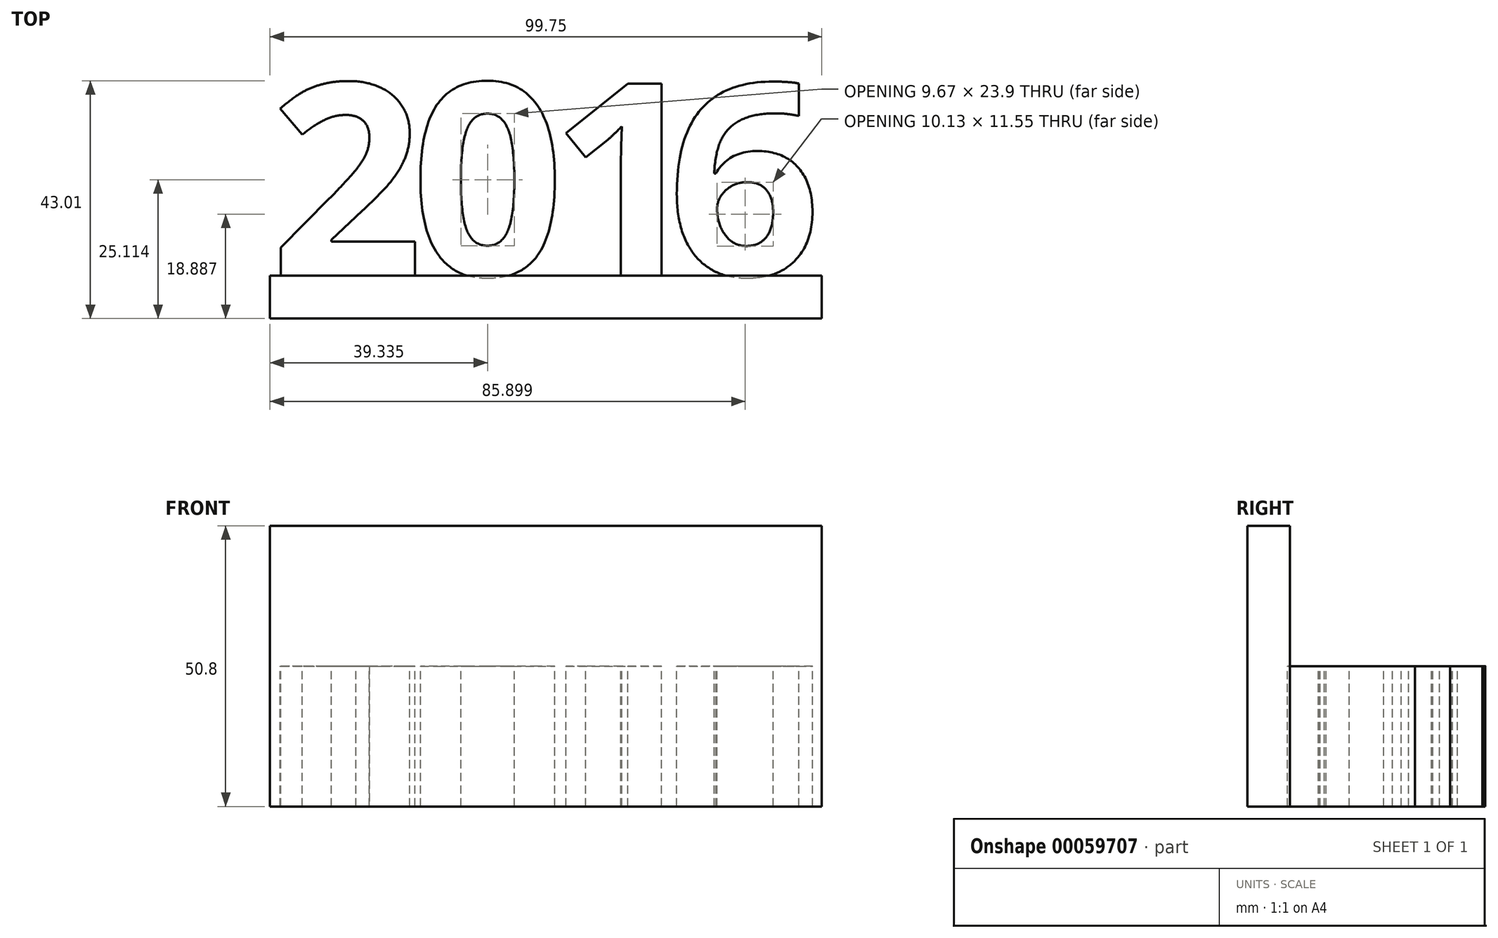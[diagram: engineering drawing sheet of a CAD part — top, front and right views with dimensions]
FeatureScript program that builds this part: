
annotation { "Feature Type Name" : "Feature", "Feature Type Description" : "" }
export const myFeature = defineFeature(function(context is Context, id is Id, definition is map)
    precondition{}
    {
        {
            var Q0;
            Q0=qCreatedBy(makeId("Top.planeOp"),FACE);
            var sketch = newSketch(context, id + "F0", { "sketchPlane" : qUnion([Q0])});
            skText(sketch, "E0", { "text": "2016", "fontName": "OpenSans-Bold.ttf"});
            const initialGuessF0  = {"E0": [0, 0, 1, 0, 0.03504]};
            skSetInitialGuess(sketch, initialGuessF0);
            skSolve(sketch);
        }
        {
            var Q0;
            Q0=makeQuery(id+"F0.imprint","IMPRINT",FACE,{"disambiguationData":[TD([[makeQuery(id+"F0.imprint","IMPRINT",EDGE,{"derivedFrom":sQuery(id+"F0.wireOp",EDGE,"E0.sketch_text.stroke-0")}),-1.0]])]});
            extrude(context, id + "F1", {"entities" : qUnion([Q0]), "oppositeDirection" : true, "depth" : 25.4 * mm});
        }
        {
            var Q0;
            Q0=makeQuery(id+"F0.imprint","IMPRINT",FACE,{"disambiguationData":[TD([[makeQuery(id+"F0.imprint","IMPRINT",EDGE,{"derivedFrom":sQuery(id+"F0.wireOp",EDGE,"E0.sketch_text.stroke-24")}),-1.0]])]});
            var Q1;
            Q1=makeQuery(id+"F0.imprint","IMPRINT",FACE,{"disambiguationData":[TD([[makeQuery(id+"F0.imprint","IMPRINT",EDGE,{"derivedFrom":sQuery(id+"F0.wireOp",EDGE,"E0.sketch_text.stroke-40")}),-1.0]])]});
            var Q2;
            Q2=makeQuery(id+"F0.imprint","IMPRINT",FACE,{"disambiguationData":[TD([[makeQuery(id+"F0.imprint","IMPRINT",EDGE,{"derivedFrom":sQuery(id+"F0.wireOp",EDGE,"E0.sketch_text.stroke-50")}),-1.0]])]});
            extrude(context, id + "F2", {"entities" : qUnion([Q0, Q1, Q2]), "operationType" : NewBodyOperationType.ADD, "oppositeDirection" : true, "depth" : 25.4 * mm});
        }
        {
            var Q0;
            Q0=makeQuery(id+"F2.opExtrude","SWEPT_BODY",BODY,{"disambiguationData":[OSD([sQuery(id+"F0.wireOp",EDGE,"E0.sketch_text.stroke-50"),sQuery(id+"F0.wireOp",EDGE,"E0.sketch_text.stroke-51"),sQuery(id+"F0.wireOp",EDGE,"E0.sketch_text.stroke-52"),sQuery(id+"F0.wireOp",EDGE,"E0.sketch_text.stroke-53"),sQuery(id+"F0.wireOp",EDGE,"E0.sketch_text.stroke-54"),sQuery(id+"F0.wireOp",EDGE,"E0.sketch_text.stroke-55"),sQuery(id+"F0.wireOp",EDGE,"E0.sketch_text.stroke-56"),sQuery(id+"F0.wireOp",EDGE,"E0.sketch_text.stroke-57"),sQuery(id+"F0.wireOp",EDGE,"E0.sketch_text.stroke-58"),sQuery(id+"F0.wireOp",EDGE,"E0.sketch_text.stroke-59"),sQuery(id+"F0.wireOp",EDGE,"E0.sketch_text.stroke-60"),sQuery(id+"F0.wireOp",EDGE,"E0.sketch_text.stroke-61"),sQuery(id+"F0.wireOp",EDGE,"E0.sketch_text.stroke-62"),sQuery(id+"F0.wireOp",EDGE,"E0.sketch_text.stroke-63"),sQuery(id+"F0.wireOp",EDGE,"E0.sketch_text.stroke-64"),sQuery(id+"F0.wireOp",EDGE,"E0.sketch_text.stroke-65"),sQuery(id+"F0.wireOp",EDGE,"E0.sketch_text.stroke-66"),sQuery(id+"F0.wireOp",EDGE,"E0.sketch_text.stroke-67"),sQuery(id+"F0.wireOp",EDGE,"E0.sketch_text.stroke-68"),sQuery(id+"F0.wireOp",EDGE,"E0.sketch_text.stroke-69"),sQuery(id+"F0.wireOp",EDGE,"E0.sketch_text.stroke-70"),sQuery(id+"F0.wireOp",EDGE,"E0.sketch_text.stroke-71"),sQuery(id+"F0.wireOp",EDGE,"E0.sketch_text.stroke-72"),sQuery(id+"F0.wireOp",EDGE,"E0.sketch_text.stroke-73"),sQuery(id+"F0.wireOp",EDGE,"E0.sketch_text.stroke-74")])]});
            transform(context, id + "F3", {"entities" : qUnion([Q0]), "transformType" : TransformType.TRANSLATION_3D, "dx" : -4.65 * mm, "dy" : 0 * mm, "dz" : 0 * mm, "makeCopy" : false});
        }
        {
            var Q0;
            Q0=makeQuery(id+"F2.opExtrude","SWEPT_BODY",BODY,{"disambiguationData":[OSD([sQuery(id+"F0.wireOp",EDGE,"E0.sketch_text.stroke-24"),sQuery(id+"F0.wireOp",EDGE,"E0.sketch_text.stroke-25"),sQuery(id+"F0.wireOp",EDGE,"E0.sketch_text.stroke-26"),sQuery(id+"F0.wireOp",EDGE,"E0.sketch_text.stroke-27"),sQuery(id+"F0.wireOp",EDGE,"E0.sketch_text.stroke-28"),sQuery(id+"F0.wireOp",EDGE,"E0.sketch_text.stroke-29"),sQuery(id+"F0.wireOp",EDGE,"E0.sketch_text.stroke-30"),sQuery(id+"F0.wireOp",EDGE,"E0.sketch_text.stroke-31"),sQuery(id+"F0.wireOp",EDGE,"E0.sketch_text.stroke-32"),sQuery(id+"F0.wireOp",EDGE,"E0.sketch_text.stroke-33"),sQuery(id+"F0.wireOp",EDGE,"E0.sketch_text.stroke-34"),sQuery(id+"F0.wireOp",EDGE,"E0.sketch_text.stroke-35"),sQuery(id+"F0.wireOp",EDGE,"E0.sketch_text.stroke-36"),sQuery(id+"F0.wireOp",EDGE,"E0.sketch_text.stroke-37"),sQuery(id+"F0.wireOp",EDGE,"E0.sketch_text.stroke-38"),sQuery(id+"F0.wireOp",EDGE,"E0.sketch_text.stroke-39")])]});
            transform(context, id + "F4", {"entities" : qUnion([Q0]), "transformType" : TransformType.TRANSLATION_3D, "dx" : -2.34 * mm, "dy" : 0 * mm, "dz" : 0 * mm, "makeCopy" : false});
        }
        {
            var Q0;
            Q0=makeQuery(id+"F2.opExtrude","SWEPT_BODY",BODY,{"disambiguationData":[OSD([sQuery(id+"F0.wireOp",EDGE,"E0.sketch_text.stroke-40"),sQuery(id+"F0.wireOp",EDGE,"E0.sketch_text.stroke-41"),sQuery(id+"F0.wireOp",EDGE,"E0.sketch_text.stroke-42"),sQuery(id+"F0.wireOp",EDGE,"E0.sketch_text.stroke-43"),sQuery(id+"F0.wireOp",EDGE,"E0.sketch_text.stroke-44"),sQuery(id+"F0.wireOp",EDGE,"E0.sketch_text.stroke-45"),sQuery(id+"F0.wireOp",EDGE,"E0.sketch_text.stroke-46"),sQuery(id+"F0.wireOp",EDGE,"E0.sketch_text.stroke-47"),sQuery(id+"F0.wireOp",EDGE,"E0.sketch_text.stroke-48"),sQuery(id+"F0.wireOp",EDGE,"E0.sketch_text.stroke-49")])]});
            transform(context, id + "F5", {"entities" : qUnion([Q0]), "transformType" : TransformType.TRANSLATION_3D, "dx" : -4.9 * mm, "dy" : 0 * mm, "dz" : 0 * mm, "makeCopy" : false});
        }
        {
            var Q0;
            Q0=makeQuery(id+"F2.opExtrude","SWEPT_BODY",BODY,{"disambiguationData":[OSD([sQuery(id+"F0.wireOp",EDGE,"E0.sketch_text.stroke-50"),sQuery(id+"F0.wireOp",EDGE,"E0.sketch_text.stroke-51"),sQuery(id+"F0.wireOp",EDGE,"E0.sketch_text.stroke-52"),sQuery(id+"F0.wireOp",EDGE,"E0.sketch_text.stroke-53"),sQuery(id+"F0.wireOp",EDGE,"E0.sketch_text.stroke-54"),sQuery(id+"F0.wireOp",EDGE,"E0.sketch_text.stroke-55"),sQuery(id+"F0.wireOp",EDGE,"E0.sketch_text.stroke-56"),sQuery(id+"F0.wireOp",EDGE,"E0.sketch_text.stroke-57"),sQuery(id+"F0.wireOp",EDGE,"E0.sketch_text.stroke-58"),sQuery(id+"F0.wireOp",EDGE,"E0.sketch_text.stroke-59"),sQuery(id+"F0.wireOp",EDGE,"E0.sketch_text.stroke-60"),sQuery(id+"F0.wireOp",EDGE,"E0.sketch_text.stroke-61"),sQuery(id+"F0.wireOp",EDGE,"E0.sketch_text.stroke-62"),sQuery(id+"F0.wireOp",EDGE,"E0.sketch_text.stroke-63"),sQuery(id+"F0.wireOp",EDGE,"E0.sketch_text.stroke-64"),sQuery(id+"F0.wireOp",EDGE,"E0.sketch_text.stroke-65"),sQuery(id+"F0.wireOp",EDGE,"E0.sketch_text.stroke-66"),sQuery(id+"F0.wireOp",EDGE,"E0.sketch_text.stroke-67"),sQuery(id+"F0.wireOp",EDGE,"E0.sketch_text.stroke-68"),sQuery(id+"F0.wireOp",EDGE,"E0.sketch_text.stroke-69"),sQuery(id+"F0.wireOp",EDGE,"E0.sketch_text.stroke-70"),sQuery(id+"F0.wireOp",EDGE,"E0.sketch_text.stroke-71"),sQuery(id+"F0.wireOp",EDGE,"E0.sketch_text.stroke-72"),sQuery(id+"F0.wireOp",EDGE,"E0.sketch_text.stroke-73"),sQuery(id+"F0.wireOp",EDGE,"E0.sketch_text.stroke-74")])]});
            transform(context, id + "F6", {"entities" : qUnion([Q0]), "transformType" : TransformType.TRANSLATION_3D, "dx" : -6.85 * mm, "dy" : 0 * mm, "dz" : 0 * mm, "makeCopy" : false});
        }
        {
            var Q0;
            Q0=qCreatedBy(makeId("Top.planeOp"),FACE);
            var sketch = newSketch(context, id + "F7", { "sketchPlane" : qUnion([Q0])});
            skLineSegment(sketch, "E1.bottom", {"start": v(0, 0) * mm, "end": v(99.75, 0) * mm});
            skLineSegment(sketch, "E1.top", {"start": v(0, -7.72) * mm, "end": v(99.75, -7.72) * mm});
            skLineSegment(sketch, "E1.left", {"start": v(0, 0) * mm, "end": v(0, -7.72) * mm});
            skLineSegment(sketch, "E1.right", {"start": v(99.75, 0) * mm, "end": v(99.75, -7.72) * mm});
            skSolve(sketch);
        }
        {
            var Q0;
            Q0=makeQuery(id+"F7.imprint","IMPRINT",FACE,{"disambiguationData":[TD([[makeQuery(id+"F7.imprint","IMPRINT",EDGE,{"derivedFrom":sQuery(id+"F7.wireOp",EDGE,"E1.bottom")}),-1.0]])]});
            extrude(context, id + "F8", {"entities" : qUnion([Q0]), "oppositeDirection" : true, "depth" : 25.4 * mm, "hasSecondDirection" : true, "secondDirectionOppositeDirection" : false, "secondDirectionDepth" : 25.4 * mm});
        }
    });
